FCSTD DOCUMENT  (FreeCAD 1.0R38642 (Git))
Label: invalid_sketch
License: All rights reserved
LicenseURL: http://en.wikipedia.org/wiki/All_rights_reserved
objects: Sketcher::SketchObject×6, PartDesign::Body×1
note: 13 computed .brp shape members not serialized (recipe doc carries the construction recipe); baked Part::Feature solids carry a one-line shape summary decoded from their .brp

FEATURE [Sketcher::SketchObject] Sketch  label="unattached"
  ArcFitTolerance = 1e-06
  FullyConstrained = true
  MakeInternals = false
  MapMode = 5
FEATURE [Sketcher::SketchObject] Sketch001  label="unconstrained"
  ArcFitTolerance = 1e-06
  AttachmentSupport = -> [XY_Plane]
  FullyConstrained = false
  MakeInternals = false
  MapMode = 5
  sketch-geometry (1):
    g0: LineSegment StartX=-51.9326 StartY=14.0267 StartZ=0 EndX=-13.8849 EndY=36.3244 EndZ=0
FEATURE [Sketcher::SketchObject] Sketch002  label="redundant"
  ArcFitTolerance = 1e-06
  AttachmentSupport = -> [XY_Plane]
  FullyConstrained = false
  MakeInternals = false
  MapMode = 5
  sketch-geometry (1):
    g0: LineSegment StartX=-74.1881 StartY=32.8872 StartZ=0 EndX=-18.4627 EndY=49.3163 EndZ=0
  constraints (1):
    c: Horizontal(g0,g0)
FEATURE [Sketcher::SketchObject] Sketch003  label="malformed"
  ArcFitTolerance = 1e-06
  AttachmentSupport = -> [XY_Plane]
  FullyConstrained = false
  MakeInternals = false
  MapMode = 5
  sketch-geometry (1):
    g0: LineSegment StartX=-98.9758 StartY=57.7739 StartZ=0 EndX=-37.5359 EndY=105.429 EndZ=0
  constraints (1):
    c: Distance(g0,g0) = 5
FEATURE [Sketcher::SketchObject] Sketch004  label="solver_error"
  ArcFitTolerance = 1e-06
  AttachmentSupport = -> [XY_Plane]
  FullyConstrained = false
  MakeInternals = false
  MapMode = 5
  sketch-geometry (1):
    g0: LineSegment StartX=-129.244 StartY=37.8741 StartZ=0 EndX=102.615 EndY=122.264 EndZ=0
  constraints (2):
    c: Angle(g-1,g0) = 0.349066
    c: Horizontal(g0)
FEATURE [Sketcher::SketchObject] Sketch005  label="conflicting"
  ArcFitTolerance = 1e-06
  AttachmentSupport = -> [XY_Plane]
  FullyConstrained = false
  MakeInternals = false
  MapMode = 5
  sketch-geometry (2):
    g0: LineSegment StartX=-140.399 StartY=25.4 StartZ=0 EndX=99.6425 EndY=25.4 EndZ=0
    g1: LineSegment StartX=-95.8347 StartY=-25.4 StartZ=0 EndX=115.631 EndY=-25.4 EndZ=0
  constraints (5):
    c: Horizontal(g0)
    c: Distance(g-1,g0) = 25.4
    c: Horizontal(g1)
    c: Distance(g1,g-1) = 25.4
    c: Distance(g0,g1) = 127
FEATURE [PartDesign::Body] Body
  AllowCompound = false
  Group = -> [Sketch,Sketch001,Sketch002,Sketch003,Sketch004,Sketch005]
  Origin = -> Origin
